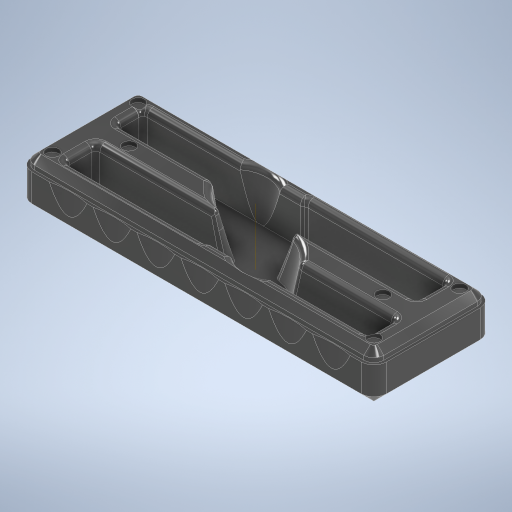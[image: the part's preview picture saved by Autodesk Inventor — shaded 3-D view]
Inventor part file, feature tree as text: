
AUTODESK INVENTOR PART (.ipt)
format: ipt  version: 2023 (Build 270158030, 158C)  size: 1,962,496 bytes
history: native  units: mm
features: projected_geometry x27, extrude x20, sketch x17, fillet x9, chamfer x5, other x4, pattern_circular x2, plane x1, pattern_linear x1, mirror x1
ambient origin geometry x8: Origin, YZ Plane, XZ Plane, XY Plane, X Axis, Y Axis, Z Axis, Center Point
bodies: Body1 (feature_tree), Body2 (feature_tree), Body3 (feature_tree)
feature tree (87):
  other  "case"
  extrude  "Extrusion1"  Depth=56.0mm
  extrude  "Extrusion2"  Depth=28.0mm
  extrude  "Extrusion3"  Depth=2.0mm
  fillet  "Fillet1"  Radius=4.0mm
  fillet  "Fillet2"  Radius=20.0mm
  fillet  "Fillet3"  Radius=4.0mm
  pattern_circular  "Circular Pattern1"  Count=2  [1 undecoded]
  fillet  "Fillet4"  Radius=96.0mm
  chamfer  "Chamfer1"  Distance=20.0mm
  extrude  "Extrusion4"  Depth=16.6mm
  chamfer  "Chamfer2"  Distance=20.0mm Angle=180.0deg
  extrude  "Extrusion5"  Depth=6.0mm TaperAngle=45.0deg
  pattern_circular  "Circular Pattern2"  [2 undecoded]
  fillet  "Fillet5"  Radius=5.0mm
  fillet  "Fillet6"  Radius=3.0mm
  fillet  "Fillet10"  Radius=6.0mm
  fillet  "Fillet11"  Radius=6.5mm
  extrude  "Extrusion6"  Depth=6.5mm
  plane  "Work Plane1"
  extrude  "Extrusion7"  Depth=22.0mm
  extrude  "Extrusion8"  Depth=2.0mm TaperAngle=0.0deg
  extrude  "Extrusion9"  Depth=20.0mm TaperAngle=360.0deg
  fillet  "Fillet8"  Radius=6.5mm
  extrude  "Extrusion10"  Depth=6.5mm
  pattern_linear  "Rectangular Pattern1"  Spacing1=2.0mm  [1 undecoded]
  mirror  "Mirror1"
  extrude  "Extrusion11"  Depth=3.0mm
  extrude  "Extrusion15"  Depth=6.5mm
  extrude  "Extrusion16"  Depth=6.45mm
  chamfer  "Chamfer4"  Distance=1.0mm
  extrude  "Extrusion18"  Depth=3.0mm TaperAngle=0.0deg
  extrude  "Extrusion19"  Depth=3.1mm TaperAngle=0.0deg
  extrude  "Extrusion12"  Depth=1.8mm TaperAngle=0.0deg
  extrude  "Extrusion13"  Depth=0.5mm
  extrude  "Extrusion14"  Depth=1.0mm TaperAngle=0.0deg
  extrude  "Extrusion17"  Depth=0.5mm
  chamfer  "Chamfer5"  Distance=80.0mm
  chamfer  "Chamfer6"  Distance=20.0mm
  extrude  "Extrusion20"  Depth=39.0mm
  sketch  "Sketch1"  dims[d0=167.0mm d1=56.0mm]
  sketch  "Sketch2"  dims[d2=83.5mm d3=28.0mm]
  projected_geometry  "Projected Loop1"
  sketch  "Sketch5"  dims[d4=24.0mm d5=0.0mm d6=2.0mm d8=4.0mm d9=20.0mm d10=4.0mm d11=20.0mm d12=96.0mm]
  projected_geometry  "Projected Loop5"
  sketch  "Sketch6"  dims[d13=67.0mm]
  other  "Work Axis1"
  sketch  "Sketch8"  dims[d14=75.0mm]
  projected_geometry  "Projected Loop7"
  other  "lid"
  sketch  "Sketch9"  dims[d15=12.0mm]
  projected_geometry  "Projected Loop8"
  sketch  "Sketch10"  dims[d16=14.3mm]
  projected_geometry  "Projected Loop9"
  sketch  "Sketch11"  dims[d17=12.4mm]
  projected_geometry  "Projected Loop10"
  sketch  "Sketch12"  dims[d18=0.95mm]
  projected_geometry  "Projected Loop11"
  sketch  "Sketch15"  dims[d19=0.95mm]
  sketch  "Sketch16"  dims[d20=2.0mm]
  other  "lid-part2"
  projected_geometry  "Projected Loop12"
  projected_geometry  "Projected Loop13"
  projected_geometry  "Projected Loop14"
  projected_geometry  "Projected Loop15"
  projected_geometry  "Projected Loop16"
  projected_geometry  "Projected Loop17"
  projected_geometry  "Projected Loop18"
  projected_geometry  "Projected Loop19"
  sketch  "Sketch18"  dims[d21=3.7mm d22=20.0mm d23=0.0mm]
  projected_geometry  "Projected Loop20"
  projected_geometry  "Projected Loop21"
  projected_geometry  "Projected Loop22"
  projected_geometry  "Projected Loop23"
  projected_geometry  "Projected Loop24"
  projected_geometry  "Projected Loop25"
  projected_geometry  "Projected Loop26"
  projected_geometry  "Projected Loop27"
  sketch  "Sketch19"  dims[d24=25.0mm d27=16.6mm d28=-1.745329mm]
  projected_geometry  "Projected Loop28"
  sketch  "Sketch20"  dims[d29=4.0mm]
  projected_geometry  "Projected Loop29"
  projected_geometry  "Projected Loop30"
  sketch  "Sketch21"  dims[d30=3.0mm]
  projected_geometry  "Projected Loop31"
  sketch  "Sketch22"  dims[d31=4.0mm d32=20.0mm d33=180.0deg]
  sketch  "Sketch23"  dims[d35=6.0mm d36=6.0mm d37=2.0mm d38=45.0deg d39=1.3mm d40=5.0mm d41=0.0mm d42=3.0mm d43=2.0mm d44=45.0deg d45=6.0mm d46=6.5mm d47=6.5mm d48=22.0mm d49=2.0mm d50=0.0mm d51=20.0mm d52=360.0deg d54=6.5mm d55=6.5mm d56=2.0mm d57=3.0mm d59=6.5mm d60=6.45mm d61=1.0mm d62=3.0mm d63=0.0mm d64=3.1mm d65=0.0mm d69=1.8mm d70=0.0mm d71=0.5mm d72=1.0mm d73=0.0mm d74=0.5mm d75=80.0mm d76=20.0mm d77=39.0mm d79=8.5mm d80=-1.047198mm d82=70.0mm d84=124.0mm d85=55.0mm d86=1.0mm d89=2.0mm d90=0.0mm d91=0.6mm d92=0.0mm d93=30.0deg d94=1.0mm d95=6.0mm d96=6.0mm d97=7.0mm d98=6.0mm d99=6.0mm d101=1.0mm d108=3.0mm d109=3.0mm d110=0.4mm d111=0.0mm d112=1.6mm d113=1.6mm d114=1.1mm d115=1.1mm d116=7.0mm d117=3.0mm d119=2.0mm d120=1.1mm d121=1.1mm d122=1.5mm d123=1.5mm d124=1.5mm d125=1.0mm d126=1.1mm d127=1.1mm d128=1.8mm d131=2.0mm d132=1.5mm d133=1.5mm d140=50.0mm d142=8.0mm d143=60.0mm d145=8.0mm d148=0.0mm d149=0.0mm d150=0.0mm d151=0.0mm d152=3.5mm d153=0.0mm d154=2.5mm d155=2.0mm d156=45.0deg d158=0.4mm d159=0.4mm d160=0.0mm d163=3.0mm d164=1.5mm d165=0.4mm d166=0.0mm d167=3.1mm d168=0.0mm d169=1.5mm d170=2.0mm d171=45.0deg d172=1.5mm d173=2.0mm d174=45.0deg d175=8.0mm d176=8.0mm d177=45.0mm d178=16.0mm d179=2.5mm d180=3.0mm d182=0.0mm d183=0.0mm d185=2.0mm]
note: 4 required parameter values undecoded (feature->parameter linkage not recoverable at this tier; creation-order binding heuristic only, values carry confidence <= 0.55)
